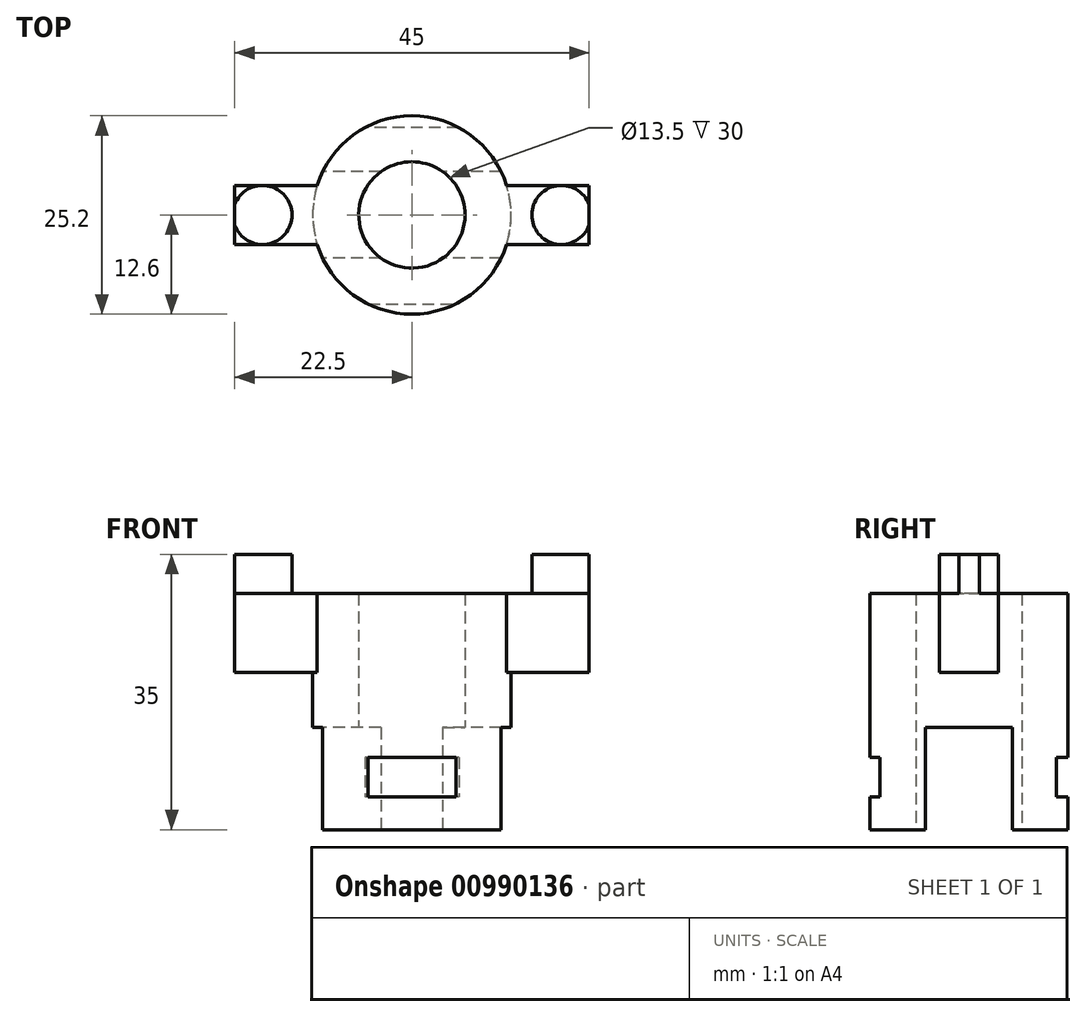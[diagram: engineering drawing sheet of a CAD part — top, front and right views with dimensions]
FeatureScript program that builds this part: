
annotation { "Feature Type Name" : "Feature", "Feature Type Description" : "" }
export const myFeature = defineFeature(function(context is Context, id is Id, definition is map)
    precondition{}
    {
        {
            var Q0;
            Q0=qCreatedBy(makeId("Top.planeOp"),FACE);
            var sketch = newSketch(context, id + "F0", { "sketchPlane" : qUnion([Q0])});
            skCircle(sketch, "E0", {"center": v(0, 0) * mm, "radius": 12.6 * mm});
            skCircle(sketch, "E1", {"center": v(0, 0) * mm, "radius": 6.75 * mm});
            skSolve(sketch);
        }
        {
            var Q0;
            Q0=makeQuery(id+"F0.imprint","IMPRINT",FACE,{"disambiguationData":[TD([[makeQuery(id+"F0.imprint","IMPRINT",EDGE,{"derivedFrom":sQuery(id+"F0.wireOp",EDGE,"E0")}),1.0]])]});
            extrude(context, id + "F1", {"entities" : qUnion([Q0]), "depth" : 30 * mm, "offsetDistance" : 25 * mm});
        }
        {
            var Q0;
            Q0=qCreatedBy(makeId("Right.planeOp"),FACE);
            var sketch = newSketch(context, id + "F2", { "sketchPlane" : qUnion([Q0])});
            skLineSegment(sketch, "E2.bottom", {"start": v(-5.5, 13) * mm, "end": v(5.5, 13) * mm});
            skLineSegment(sketch, "E2.top", {"start": v(-5.5, 0) * mm, "end": v(5.5, 0) * mm});
            skLineSegment(sketch, "E2.left", {"start": v(-5.5, 13) * mm, "end": v(-5.5, 0) * mm});
            skLineSegment(sketch, "E2.right", {"start": v(5.5, 13) * mm, "end": v(5.5, 0) * mm});
            skSolve(sketch);
        }
        {
            var Q0;
            Q0=makeQuery(id+"F2.imprint","IMPRINT",FACE,{"disambiguationData":[TD([[makeQuery(id+"F2.imprint","IMPRINT",EDGE,{"derivedFrom":sQuery(id+"F2.wireOp",EDGE,"E2.bottom")}),-1.0]])]});
            extrude(context, id + "F3", {"entities" : qUnion([Q0]), "endBound" : BoundingType.SYMMETRIC, "depth" : 30 * mm, "offsetDistance" : 25 * mm});
        }
        {
            var Q0;
            Q0=makeQuery(id+"F3.opExtrude","SWEPT_BODY",BODY,{"disambiguationData":[OSD([sQuery(id+"F2.wireOp",EDGE,"E2.bottom"),sQuery(id+"F2.wireOp",EDGE,"E2.top"),sQuery(id+"F2.wireOp",EDGE,"E2.left"),sQuery(id+"F2.wireOp",EDGE,"E2.right")])]});
            var Q1;
            Q1=makeQuery(id+"F1.opExtrude","SWEPT_BODY",BODY,{"disambiguationData":[OSD([sQuery(id+"F0.wireOp",EDGE,"E0"),sQuery(id+"F0.wireOp",EDGE,"E1")])]});
            booleanBodies(context, id + "F4", {"operationType" : BooleanOperationType.SUBTRACTION, "tools" : qUnion([Q0]), "targets" : qUnion([Q1])});
        }
        {
            var Q0;
            Q0=qCreatedBy(makeId("Right.planeOp"),FACE);
            var sketch = newSketch(context, id + "F5", { "sketchPlane" : qUnion([Q0])});
            skLineSegment(sketch, "E3.bottom", {"start": v(-12.6, 9.2) * mm, "end": v(-11.3, 9.2) * mm});
            skLineSegment(sketch, "E3.top", {"start": v(-12.6, 4.2) * mm, "end": v(-11.3, 4.2) * mm});
            skLineSegment(sketch, "E3.left", {"start": v(-12.6, 9.2) * mm, "end": v(-12.6, 4.2) * mm});
            skLineSegment(sketch, "E3.right", {"start": v(-11.3, 9.2) * mm, "end": v(-11.3, 4.2) * mm});
            skSolve(sketch);
        }
        {
            var Q0;
            Q0 = qSketchRegion(id + "F5", true);
            extrude(context, id + "F6", {"entities" : qUnion([Q0]), "operationType" : NewBodyOperationType.REMOVE, "endBound" : BoundingType.SYMMETRIC, "oppositeDirection" : true, "depth" : 25 * mm, "offsetDistance" : 25 * mm});
        }
        {
            var Q0;
            Q0=qCreatedBy(makeId("Right.planeOp"),FACE);
            var sketch = newSketch(context, id + "F7", { "sketchPlane" : qUnion([Q0])});
            skLineSegment(sketch, "E4.bottom", {"start": v(11.1, 9.2) * mm, "end": v(12.6, 9.2) * mm});
            skLineSegment(sketch, "E4.top", {"start": v(11.1, 4.2) * mm, "end": v(12.6, 4.2) * mm});
            skLineSegment(sketch, "E4.left", {"start": v(11.1, 9.2) * mm, "end": v(11.1, 4.2) * mm});
            skLineSegment(sketch, "E4.right", {"start": v(12.6, 9.2) * mm, "end": v(12.6, 4.2) * mm});
            skSolve(sketch);
        }
        {
            var Q0;
            Q0 = qSketchRegion(id + "F7", true);
            extrude(context, id + "F8", {"entities" : qUnion([Q0]), "operationType" : NewBodyOperationType.REMOVE, "endBound" : BoundingType.SYMMETRIC, "depth" : 25 * mm, "offsetDistance" : 25 * mm});
        }
        {
            var Q0;
            Q0=makeQuery(id+"F1.opExtrude","CAP_FACE",FACE,{"disambiguationData":[OSD([sQuery(id+"F0.wireOp",EDGE,"E0"),sQuery(id+"F0.wireOp",EDGE,"E1")])],"isStart":false});
            var sketch = newSketch(context, id + "F9", { "sketchPlane" : qUnion([Q0])});
            skLineSegment(sketch, "E5.bottom", {"start": v(-22.5, 3.75) * mm, "end": v(-7.5, 3.75) * mm});
            skLineSegment(sketch, "E5.top", {"start": v(-22.5, -3.75) * mm, "end": v(-7.5, -3.75) * mm});
            skLineSegment(sketch, "E5.left", {"start": v(-22.5, 3.75) * mm, "end": v(-22.5, -3.75) * mm});
            skLineSegment(sketch, "E5.right", {"start": v(-7.5, 3.75) * mm, "end": v(-7.5, -3.75) * mm});
            skLineSegment(sketch, "E6.bottom", {"start": v(7.5, 3.75) * mm, "end": v(22.5, 3.75) * mm});
            skLineSegment(sketch, "E6.top", {"start": v(7.5, -3.75) * mm, "end": v(22.5, -3.75) * mm});
            skLineSegment(sketch, "E6.left", {"start": v(7.5, 3.75) * mm, "end": v(7.5, -3.75) * mm});
            skLineSegment(sketch, "E6.right", {"start": v(22.5, 3.75) * mm, "end": v(22.5, -3.75) * mm});
            skSolve(sketch);
        }
        {
            var Q0;
            {var subQ0=sQuery(id+"F9.wireOp",EDGE,"E5.left");Q0=makeQuery(id+"F9.imprint","IMPRINT",FACE,{"disambiguationData":[TD([[makeQuery(id+"F9.imprint","IMPRINT",EDGE,{"derivedFrom":subQ0}),1.0]])]});}
            var Q1;
            {var subQ0=sQuery(id+"F9.wireOp",EDGE,"E6.right");Q1=makeQuery(id+"F9.imprint","IMPRINT",FACE,{"disambiguationData":[TD([[makeQuery(id+"F9.imprint","IMPRINT",EDGE,{"derivedFrom":subQ0}),-1.0]])]});}
            extrude(context, id + "F10", {"entities" : qUnion([Q0, Q1]), "operationType" : NewBodyOperationType.ADD, "oppositeDirection" : true, "depth" : 10 * mm, "offsetDistance" : 25 * mm});
        }
        {
            var Q0;
            {var subQ0=sQuery(id+"F0.wireOp",EDGE,"E0");Q0=makeQuery(id+"F10.boolean.opBoolean","MERGE",FACE,{"derivedFrom":[makeQuery(id+"F1.opExtrude","CAP_FACE",FACE,{"disambiguationData":[OSD([subQ0,sQuery(id+"F0.wireOp",EDGE,"E1")])],"isStart":false}),makeQuery(id+"F10.opExtrude","CAP_FACE",FACE,{"disambiguationData":[OSD([subQ0,sQuery(id+"F9.wireOp",EDGE,"E5.bottom"),sQuery(id+"F9.wireOp",EDGE,"E5.top"),sQuery(id+"F9.wireOp",EDGE,"E5.left")])],"isStart":true}),makeQuery(id+"F10.opExtrude","CAP_FACE",FACE,{"disambiguationData":[OSD([subQ0,sQuery(id+"F9.wireOp",EDGE,"E6.bottom"),sQuery(id+"F9.wireOp",EDGE,"E6.top"),sQuery(id+"F9.wireOp",EDGE,"E6.right")])],"isStart":true})]});}
            var sketch = newSketch(context, id + "F11", { "sketchPlane" : qUnion([Q0])});
            skCircle(sketch, "E7", {"center": v(-18.98, 0) * mm, "radius": 3.75 * mm});
            skCircle(sketch, "E8", {"center": v(18.98, 0) * mm, "radius": 3.75 * mm});
            skSolve(sketch);
        }
        {
            var Q0;
            {var subQ0=sQuery(id+"F11.wireOp",EDGE,"E7");var subQ1=makeQuery(id+"F10.opExtrude","CAP_EDGE",EDGE,{"disambiguationData":[OSD([sQuery(id+"F9.wireOp",EDGE,"E5.left")])],"isStart":true});var subQ2=makeQuery(id+"F11.imprint","INTERSECT",VERTEX,{"disambiguationData":[OD(0.0)],"derivedFrom":[subQ1,subQ0]});Q0=makeQuery(id+"F11.imprint","IMPRINT",FACE,{"disambiguationData":[TD([[makeQuery(id+"F11.imprint","IMPRINT",EDGE,{"disambiguationData":[TD([[subQ2,1.0]])],"derivedFrom":subQ0}),1.0]])]});}
            var Q1;
            {var subQ0=sQuery(id+"F11.wireOp",EDGE,"E8");var subQ1=makeQuery(id+"F11.imprint","INTERSECT",VERTEX,{"derivedFrom":[makeQuery(id+"F10.opExtrude","CAP_EDGE",EDGE,{"disambiguationData":[OSD([sQuery(id+"F9.wireOp",EDGE,"E6.bottom")])],"isStart":true}),subQ0]});Q1=makeQuery(id+"F11.imprint","IMPRINT",FACE,{"disambiguationData":[TD([[makeQuery(id+"F11.imprint","IMPRINT",EDGE,{"disambiguationData":[TD([[subQ1,1.0]])],"derivedFrom":subQ0}),1.0]])]});}
            extrude(context, id + "F12", {"entities" : qUnion([Q0, Q1]), "operationType" : NewBodyOperationType.ADD, "depth" : 5 * mm, "offsetDistance" : 25 * mm});
        }
    });
